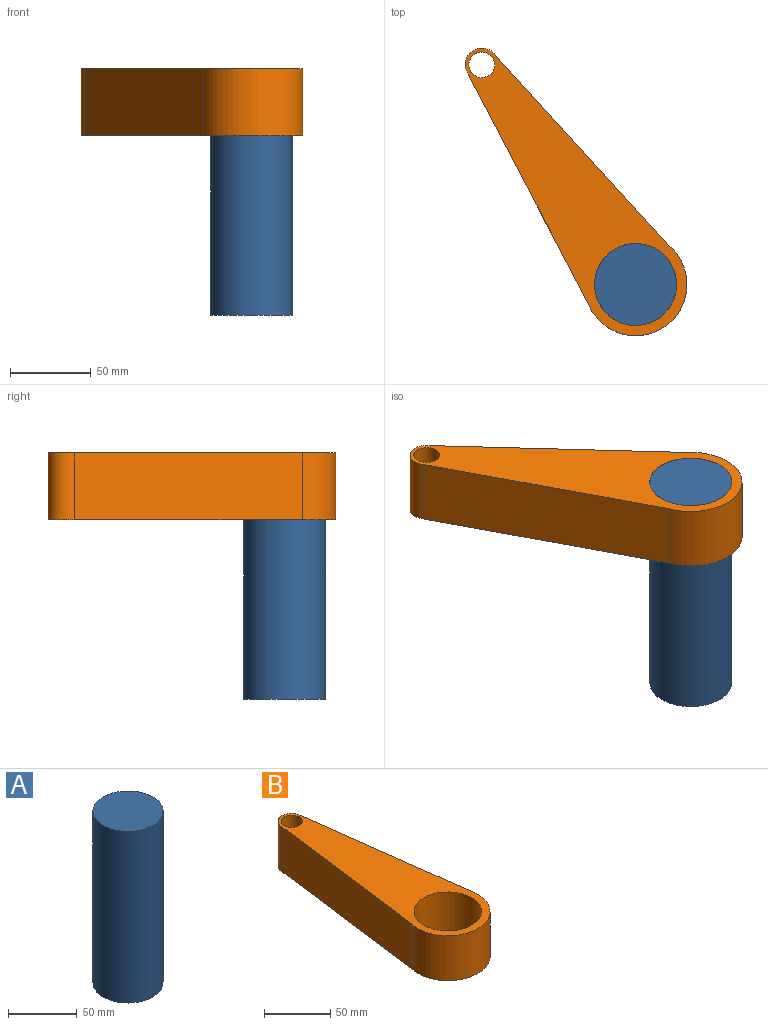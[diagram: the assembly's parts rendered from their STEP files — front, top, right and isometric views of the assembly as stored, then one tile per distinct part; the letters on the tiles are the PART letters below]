
ASSEMBLY  parts=2 mates=1
PART A: 3 faces, bbox 50.8x50.8x152.4 mm
  f0: cylinder r=25.4mm len=152.4mm, axis (0,0,-1), area 24322mm2, adj f1,f2
  f1: plane 50.8x50.8mm, normal (0,0,1), area 2026.8mm2, adj f0
  f2: plane 50.8x50.8mm, normal (0,0,-1), area 2026.8mm2, adj f0
PART B: 8 faces, bbox 63.5x208.2x41.3 mm
  f0: cylinder r=31.75mm len=63.5mm, axis (0,0,-1), area 4789.6mm2, adj f1,f3,f4,f5
  f1: plane 158.06x41.28mm, normal (0.99,0.13,0), area 6577.9mm2, adj f0,f2,f4,f5
  f2: cylinder r=10.32mm len=41.28mm, axis (0,0,-1), area 1338mm2, adj f1,f3,f4,f5
  f3: plane 158.06x41.28mm, normal (-0.99,0.13,0), area 6577.9mm2, adj f0,f2,f4,f5
  f4: plane 208.18x63.5mm, normal (0,0,1), area 6517.1mm2, adj f0,f1,f2,f3,f6,f7
  f5: plane 208.18x63.5mm, normal (0,0,-1), area 6517.1mm2, adj f0,f1,f2,f3,f6,f7
  f6: cylinder r=25.4mm len=50.8mm, axis (0,0,1), area 6587.2mm2, adj f4,f5
  f7: cylinder r=7.94mm len=41.28mm, axis (0,0,1), area 2058.5mm2, adj f4,f5
PLACE A rot(axis=(1,0,0),180deg) t=(0,0,0)mm fixed
PLACE B rot(axis=(0,0,1),35deg) t=(0,0,-41.28)mm
MATE revolute A.f0 <-> B.f6  axis (0,0,1) through (0,0,0)mm
